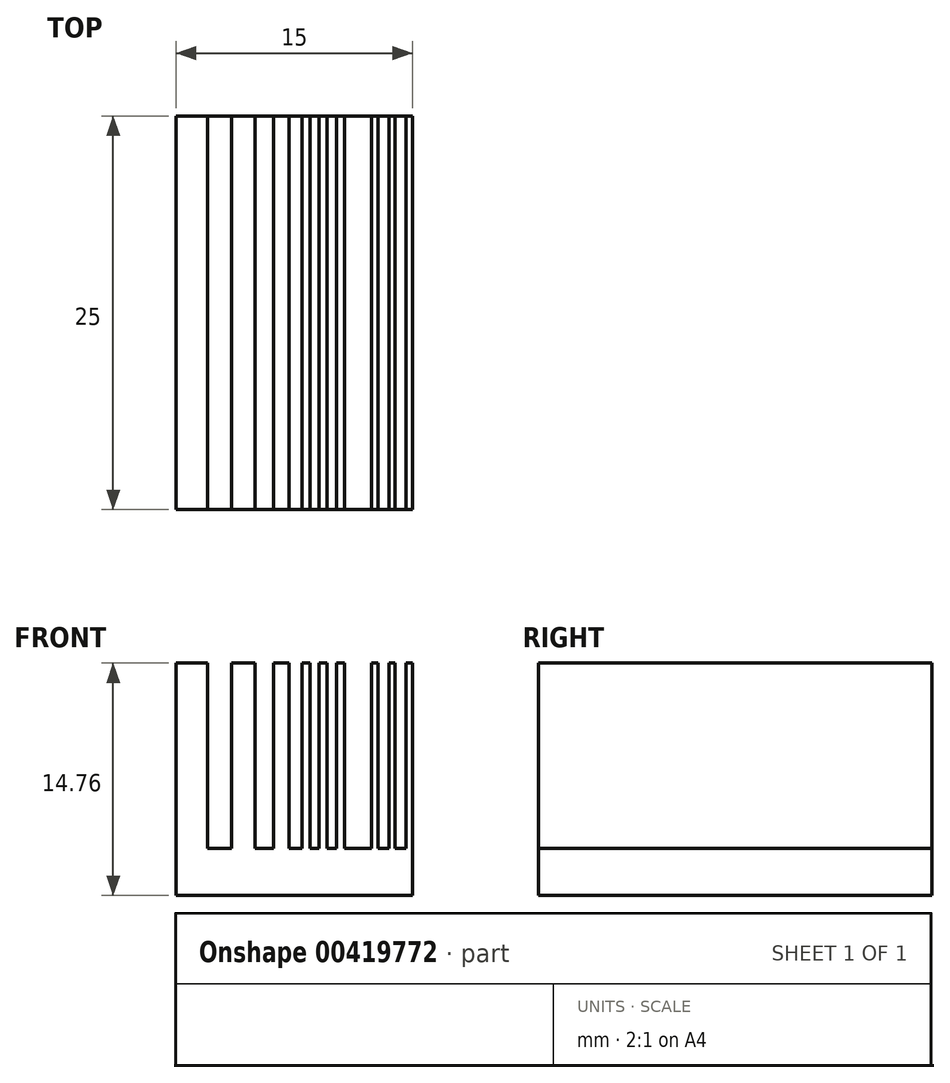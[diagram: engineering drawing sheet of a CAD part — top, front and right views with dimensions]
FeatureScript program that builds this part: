
annotation { "Feature Type Name" : "Feature", "Feature Type Description" : "" }
export const myFeature = defineFeature(function(context is Context, id is Id, definition is map)
    precondition{}
    {
        {
            var Q0;
            Q0=qCreatedBy(makeId("Front.planeOp"),FACE);
            var sketch = newSketch(context, id + "F0", { "sketchPlane" : qUnion([Q0])});
            skLineSegment(sketch, "E0.bottom", {"start": v(-44.62, -17.8) * mm, "end": v(56.98, -17.8) * mm});
            skLineSegment(sketch, "E0.top", {"start": v(-44.62, -22.89) * mm, "end": v(56.98, -22.89) * mm});
            skLineSegment(sketch, "E0.left", {"start": v(-44.62, -17.8) * mm, "end": v(-44.62, -22.89) * mm});
            skLineSegment(sketch, "E0.right", {"start": v(56.98, -17.8) * mm, "end": v(56.98, -22.89) * mm});
            skLineSegment(sketch, "E1.bottom", {"start": v(56.98, -17.8) * mm, "end": v(51.9, -17.8) * mm});
            skLineSegment(sketch, "E1.top", {"start": v(56.98, 7.6) * mm, "end": v(51.9, 7.6) * mm});
            skLineSegment(sketch, "E1.left", {"start": v(56.98, -17.8) * mm, "end": v(56.98, 7.6) * mm});
            skLineSegment(sketch, "E1.right", {"start": v(51.9, -17.8) * mm, "end": v(51.9, 7.6) * mm});
            skLineSegment(sketch, "E2.bottom", {"start": v(-44.62, -17.8) * mm, "end": v(-39.54, -17.8) * mm});
            skLineSegment(sketch, "E2.top", {"start": v(-44.62, 7.6) * mm, "end": v(-39.54, 7.6) * mm});
            skLineSegment(sketch, "E2.left", {"start": v(-44.62, -17.8) * mm, "end": v(-44.62, 7.6) * mm});
            skLineSegment(sketch, "E2.right", {"start": v(-39.54, -17.8) * mm, "end": v(-39.54, 7.6) * mm});
            skLineSegment(sketch, "E3.bottom", {"start": v(-20.37, 7.6) * mm, "end": v(-17.83, 7.6) * mm});
            skLineSegment(sketch, "E3.top", {"start": v(-20.37, -17.8) * mm, "end": v(-17.83, -17.8) * mm});
            skLineSegment(sketch, "E3.left", {"start": v(-20.37, 7.6) * mm, "end": v(-20.37, -17.8) * mm});
            skLineSegment(sketch, "E3.right", {"start": v(-17.83, 7.6) * mm, "end": v(-17.83, -17.8) * mm});
            skLineSegment(sketch, "E4.bottom", {"start": v(3.05, 7.6) * mm, "end": v(8.13, 7.6) * mm});
            skLineSegment(sketch, "E4.top", {"start": v(3.05, -17.8) * mm, "end": v(8.13, -17.8) * mm});
            skLineSegment(sketch, "E4.left", {"start": v(3.05, 7.6) * mm, "end": v(3.05, -17.8) * mm});
            skLineSegment(sketch, "E4.right", {"start": v(8.13, 7.6) * mm, "end": v(8.13, -17.8) * mm});
            skLineSegment(sketch, "E5.bottom", {"start": v(22.11, 7.6) * mm, "end": v(25.92, 7.6) * mm});
            skLineSegment(sketch, "E5.top", {"start": v(22.11, -17.8) * mm, "end": v(25.92, -17.8) * mm});
            skLineSegment(sketch, "E5.left", {"start": v(22.11, 7.6) * mm, "end": v(22.11, -17.8) * mm});
            skLineSegment(sketch, "E5.right", {"start": v(25.92, 7.6) * mm, "end": v(25.92, -17.8) * mm});
            skLineSegment(sketch, "E6.bottom", {"start": v(38.11, 7.6) * mm, "end": v(40.65, 7.6) * mm});
            skLineSegment(sketch, "E6.top", {"start": v(38.11, -17.8) * mm, "end": v(40.65, -17.8) * mm});
            skLineSegment(sketch, "E6.left", {"start": v(38.11, 7.6) * mm, "end": v(38.11, -17.8) * mm});
            skLineSegment(sketch, "E6.right", {"start": v(40.65, 7.6) * mm, "end": v(40.65, -17.8) * mm});
            skLineSegment(sketch, "E7.bottom", {"start": v(-31.28, 7.6) * mm, "end": v(-27.47, 7.6) * mm});
            skLineSegment(sketch, "E7.top", {"start": v(-31.28, -17.8) * mm, "end": v(-27.47, -17.8) * mm});
            skLineSegment(sketch, "E7.left", {"start": v(-31.28, 7.6) * mm, "end": v(-31.28, -17.8) * mm});
            skLineSegment(sketch, "E7.right", {"start": v(-27.47, 7.6) * mm, "end": v(-27.47, -17.8) * mm});
            skSolve(sketch);
        }
        {
            var Q0;
            Q0=makeQuery(id+"F0.imprint","IMPRINT",FACE,{"disambiguationData":[TD([[makeQuery(id+"F0.imprint","IMPRINT",EDGE,{"derivedFrom":sQuery(id+"F0.wireOp",EDGE,"E0.top")}),1.0]])]});
            var Q1;
            Q1=makeQuery(id+"F0.imprint","IMPRINT",FACE,{"disambiguationData":[TD([[makeQuery(id+"F0.imprint","IMPRINT",EDGE,{"derivedFrom":sQuery(id+"F0.wireOp",EDGE,"E1.bottom")}),-1.0]])]});
            var Q2;
            Q2=makeQuery(id+"F0.imprint","IMPRINT",FACE,{"disambiguationData":[TD([[makeQuery(id+"F0.imprint","IMPRINT",EDGE,{"derivedFrom":sQuery(id+"F0.wireOp",EDGE,"E6.bottom")}),-1.0]])]});
            var Q3;
            Q3=makeQuery(id+"F0.imprint","IMPRINT",FACE,{"disambiguationData":[TD([[makeQuery(id+"F0.imprint","IMPRINT",EDGE,{"derivedFrom":sQuery(id+"F0.wireOp",EDGE,"E5.bottom")}),-1.0]])]});
            var Q4;
            Q4=makeQuery(id+"F0.imprint","IMPRINT",FACE,{"disambiguationData":[TD([[makeQuery(id+"F0.imprint","IMPRINT",EDGE,{"derivedFrom":sQuery(id+"F0.wireOp",EDGE,"E4.bottom")}),-1.0]])]});
            var Q5;
            Q5=makeQuery(id+"F0.imprint","IMPRINT",FACE,{"disambiguationData":[TD([[makeQuery(id+"F0.imprint","IMPRINT",EDGE,{"derivedFrom":sQuery(id+"F0.wireOp",EDGE,"E7.bottom")}),-1.0]])]});
            var Q6;
            Q6=makeQuery(id+"F0.imprint","IMPRINT",FACE,{"disambiguationData":[TD([[makeQuery(id+"F0.imprint","IMPRINT",EDGE,{"derivedFrom":sQuery(id+"F0.wireOp",EDGE,"E2.bottom")}),1.0]])]});
            var Q7;
            Q7=makeQuery(id+"F0.imprint","IMPRINT",FACE,{"disambiguationData":[TD([[makeQuery(id+"F0.imprint","IMPRINT",EDGE,{"derivedFrom":sQuery(id+"F0.wireOp",EDGE,"E3.bottom")}),-1.0]])]});
            extrude(context, id + "F1", {"entities" : qUnion([Q0, Q1, Q2, Q3, Q4, Q5, Q6, Q7]), "depth" : 40 * mm});
        }
        {
            var Q0;
            Q0=makeQuery(id+"F1.opExtrude","SWEPT_BODY",BODY,{"disambiguationData":[OSD([sQuery(id+"F0.wireOp",EDGE,"E0.bottom"),sQuery(id+"F0.wireOp",EDGE,"E0.top"),sQuery(id+"F0.wireOp",EDGE,"E0.left"),sQuery(id+"F0.wireOp",EDGE,"E0.right"),sQuery(id+"F0.wireOp",EDGE,"E1.top"),sQuery(id+"F0.wireOp",EDGE,"E1.left"),sQuery(id+"F0.wireOp",EDGE,"E1.right"),sQuery(id+"F0.wireOp",EDGE,"E2.top"),sQuery(id+"F0.wireOp",EDGE,"E2.left"),sQuery(id+"F0.wireOp",EDGE,"E2.right"),sQuery(id+"F0.wireOp",EDGE,"E3.bottom"),sQuery(id+"F0.wireOp",EDGE,"E3.left"),sQuery(id+"F0.wireOp",EDGE,"E3.right"),sQuery(id+"F0.wireOp",EDGE,"E4.bottom"),sQuery(id+"F0.wireOp",EDGE,"E4.left"),sQuery(id+"F0.wireOp",EDGE,"E4.right"),sQuery(id+"F0.wireOp",EDGE,"E5.bottom"),sQuery(id+"F0.wireOp",EDGE,"E5.left"),sQuery(id+"F0.wireOp",EDGE,"E5.right"),sQuery(id+"F0.wireOp",EDGE,"E6.bottom"),sQuery(id+"F0.wireOp",EDGE,"E6.left"),sQuery(id+"F0.wireOp",EDGE,"E6.right"),sQuery(id+"F0.wireOp",EDGE,"E7.bottom"),sQuery(id+"F0.wireOp",EDGE,"E7.left"),sQuery(id+"F0.wireOp",EDGE,"E7.right")])]});
            deleteBodies(context, id + "F2", {"entities" : qUnion([Q0])});
        }
        {
            var Q0;
            Q0=qCreatedBy(makeId("Front.planeOp"),FACE);
            var sketch = newSketch(context, id + "F3", { "sketchPlane" : qUnion([Q0])});
            skLineSegment(sketch, "E8.bottom", {"start": v(-15.04, -11.76) * mm, "end": v(-0.04, -11.76) * mm});
            skLineSegment(sketch, "E8.top", {"start": v(-15.04, -14.76) * mm, "end": v(-0.04, -14.76) * mm});
            skLineSegment(sketch, "E8.left", {"start": v(-15.04, -11.76) * mm, "end": v(-15.04, -14.76) * mm});
            skLineSegment(sketch, "E8.right", {"start": v(-0.04, -11.76) * mm, "end": v(-0.04, -14.76) * mm});
            skLineSegment(sketch, "E9.bottom", {"start": v(-15.04, 0) * mm, "end": v(-13.04, 0) * mm});
            skLineSegment(sketch, "E9.top", {"start": v(-15.04, -11.76) * mm, "end": v(-13.04, -11.76) * mm});
            skLineSegment(sketch, "E9.left", {"start": v(-15.04, 0) * mm, "end": v(-15.04, -11.76) * mm});
            skLineSegment(sketch, "E9.right", {"start": v(-13.04, 0) * mm, "end": v(-13.04, -11.76) * mm});
            skLineSegment(sketch, "E10.bottom", {"start": v(-11.54, 0) * mm, "end": v(-10.04, 0) * mm});
            skLineSegment(sketch, "E10.top", {"start": v(-11.54, -11.76) * mm, "end": v(-10.04, -11.76) * mm});
            skLineSegment(sketch, "E10.left", {"start": v(-11.54, 0) * mm, "end": v(-11.54, -11.76) * mm});
            skLineSegment(sketch, "E10.right", {"start": v(-10.04, 0) * mm, "end": v(-10.04, -11.76) * mm});
            skLineSegment(sketch, "E11.bottom", {"start": v(-8.87, 0) * mm, "end": v(-7.87, 0) * mm});
            skLineSegment(sketch, "E11.top", {"start": v(-8.87, -11.76) * mm, "end": v(-7.87, -11.76) * mm});
            skLineSegment(sketch, "E11.left", {"start": v(-8.87, 0) * mm, "end": v(-8.87, -11.76) * mm});
            skLineSegment(sketch, "E11.right", {"start": v(-7.87, 0) * mm, "end": v(-7.87, -11.76) * mm});
            skLineSegment(sketch, "E12.bottom", {"start": v(-7.05, 0) * mm, "end": v(-6.55, 0) * mm});
            skLineSegment(sketch, "E12.top", {"start": v(-7.05, -11.76) * mm, "end": v(-6.55, -11.76) * mm});
            skLineSegment(sketch, "E12.left", {"start": v(-7.05, 0) * mm, "end": v(-7.05, -11.76) * mm});
            skLineSegment(sketch, "E12.right", {"start": v(-6.55, 0) * mm, "end": v(-6.55, -11.76) * mm});
            skLineSegment(sketch, "E13.bottom", {"start": v(-2.64, 0) * mm, "end": v(-2.24, 0) * mm});
            skLineSegment(sketch, "E13.top", {"start": v(-2.64, -11.76) * mm, "end": v(-2.24, -11.76) * mm});
            skLineSegment(sketch, "E13.left", {"start": v(-2.64, 0) * mm, "end": v(-2.64, -11.76) * mm});
            skLineSegment(sketch, "E13.right", {"start": v(-2.24, 0) * mm, "end": v(-2.24, -11.76) * mm});
            skLineSegment(sketch, "E14.1.0.0", {"start": v(-5.95, 0) * mm, "end": v(-5.95, -11.76) * mm});
            skLineSegment(sketch, "E14.1.0.1", {"start": v(-5.45, 0) * mm, "end": v(-5.45, -11.76) * mm});
            skLineSegment(sketch, "E14.1.0.2", {"start": v(-5.95, 0) * mm, "end": v(-5.45, 0) * mm});
            skLineSegment(sketch, "E14.1.0.3", {"start": v(-5.95, -11.76) * mm, "end": v(-5.45, -11.76) * mm});
            skLineSegment(sketch, "E14.2.0.0", {"start": v(-4.85, 0) * mm, "end": v(-4.85, -11.76) * mm});
            skLineSegment(sketch, "E14.2.0.1", {"start": v(-4.35, 0) * mm, "end": v(-4.35, -11.76) * mm});
            skLineSegment(sketch, "E14.2.0.2", {"start": v(-4.85, 0) * mm, "end": v(-4.35, 0) * mm});
            skLineSegment(sketch, "E14.2.0.3", {"start": v(-4.85, -11.76) * mm, "end": v(-4.35, -11.76) * mm});
            skLineSegment(sketch, "E14.direction1", {"start": v(-7.05, -11.76) * mm, "end": v(-5.95, -11.76) * mm, "construction": true});
            skLineSegment(sketch, "E15.1.0.0", {"start": v(-1.14, 0) * mm, "end": v(-1.14, -11.76) * mm});
            skLineSegment(sketch, "E15.1.0.1", {"start": v(-1.54, 0) * mm, "end": v(-1.54, -11.76) * mm});
            skLineSegment(sketch, "E15.1.0.2", {"start": v(-1.54, 0) * mm, "end": v(-1.14, 0) * mm});
            skLineSegment(sketch, "E15.1.0.3", {"start": v(-1.54, -11.76) * mm, "end": v(-1.14, -11.76) * mm});
            skLineSegment(sketch, "E15.2.0.0", {"start": v(-0.04, 0) * mm, "end": v(-0.04, -11.76) * mm});
            skLineSegment(sketch, "E15.2.0.1", {"start": v(-0.44, 0) * mm, "end": v(-0.44, -11.76) * mm});
            skLineSegment(sketch, "E15.2.0.2", {"start": v(-0.44, 0) * mm, "end": v(-0.04, 0) * mm});
            skLineSegment(sketch, "E15.2.0.3", {"start": v(-0.44, -11.76) * mm, "end": v(-0.04, -11.76) * mm});
            skLineSegment(sketch, "E15.direction1", {"start": v(-2.64, -11.76) * mm, "end": v(-1.54, -11.76) * mm, "construction": true});
            skSolve(sketch);
        }
        {
            var Q0;
            Q0=qSketchRegion(id+"F3",true);
            extrude(context, id + "F4", {"entities" : qUnion([Q0]), "depth" : 25 * mm, "symmetric" : true});
        }
    });
